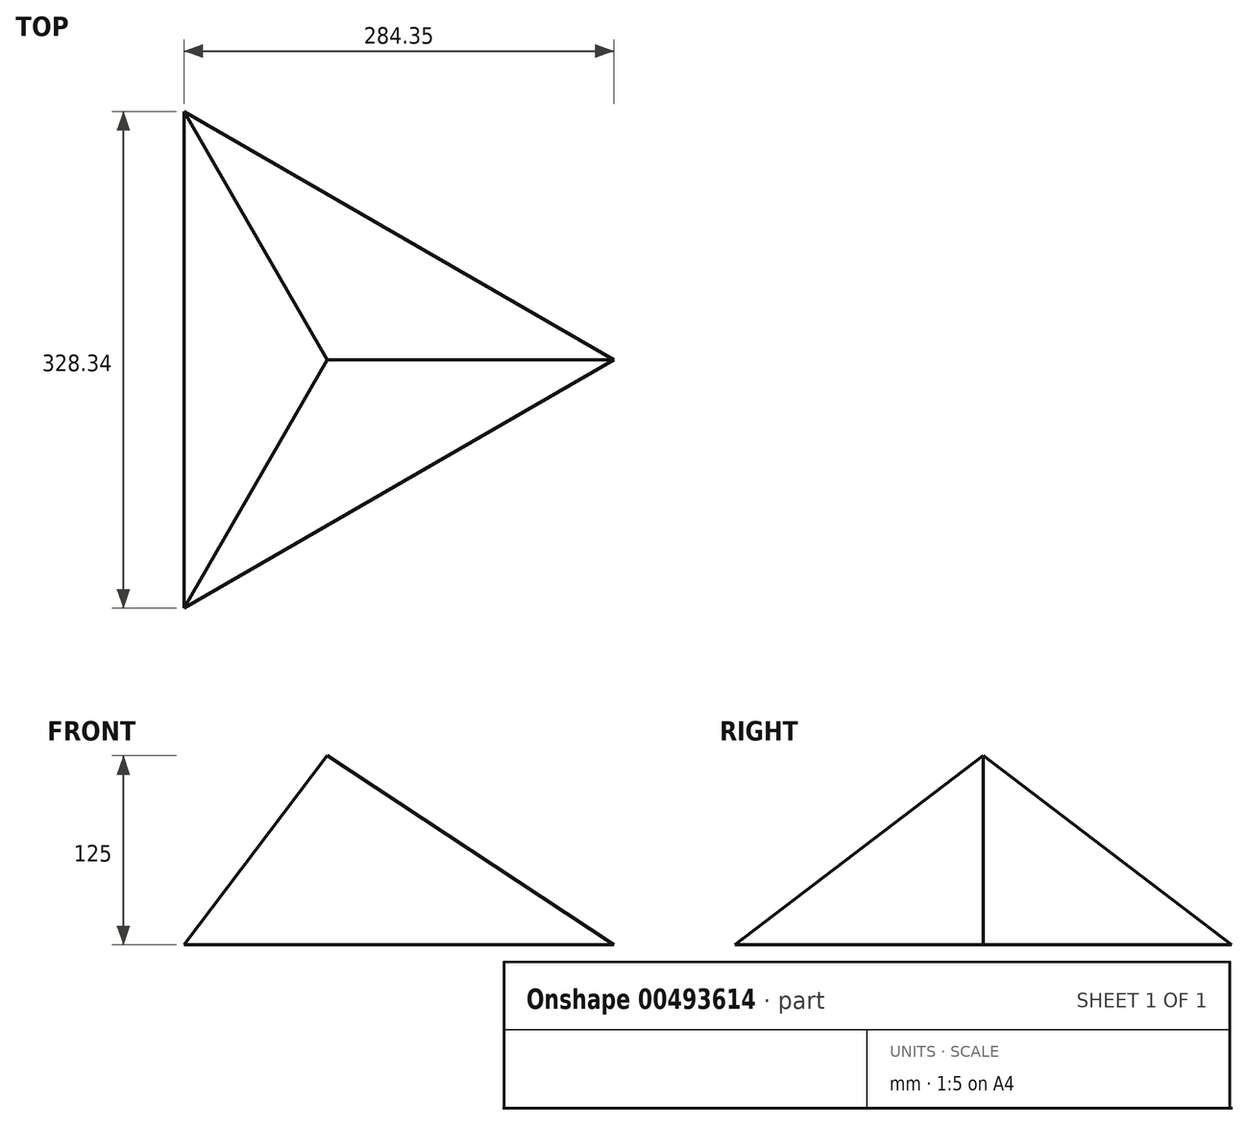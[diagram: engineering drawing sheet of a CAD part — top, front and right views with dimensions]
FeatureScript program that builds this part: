
annotation { "Feature Type Name" : "Feature", "Feature Type Description" : "" }
export const myFeature = defineFeature(function(context is Context, id is Id, definition is map)
    precondition{}
    {
        {
            var Q0;
            Q0=qCreatedBy(makeId("Top.planeOp"),FACE);
            var sketch = newSketch(context, id + "F0", { "sketchPlane" : qUnion([Q0])});
            skCircle(sketch, "E0.cCircle", {"center": v(0, 0) * mm, "radius": 189.57 * mm, "construction": true});
            skLineSegment(sketch, "E0.0", {"start": v(189.57, 0) * mm, "end": v(-94.78, -164.17) * mm});
            skLineSegment(sketch, "E0.1", {"start": v(-94.78, -164.17) * mm, "end": v(-94.78, 164.17) * mm});
            skLineSegment(sketch, "E0.2", {"start": v(-94.78, 164.17) * mm, "end": v(189.57, 0) * mm});
            skSolve(sketch);
        }
        {
            var Q0;
            Q0=qCreatedBy(makeId("Top.planeOp"),FACE);
            cPlane(context, id + "F1", {"entities" : qUnion([Q0]), "cplaneType" : CPlaneType.OFFSET, "offset" : 125 * mm, "width" : 150 * mm, "height" : 150 * mm});
        }
        {
            var Q0;
            Q0=qCreatedBy(id+"F1.planeOp",FACE);
            var sketch = newSketch(context, id + "F2", { "sketchPlane" : qUnion([Q0])});
            skPoint(sketch, "E1", {"position": v(0, 0) * mm});
            skSolve(sketch);
        }
        {
            var Q0;
            Q0=makeQuery(id+"F0.imprint","IMPRINT",FACE,{"disambiguationData":[TD([[makeQuery(id+"F0.imprint","IMPRINT",EDGE,{"derivedFrom":sQuery(id+"F0.wireOp",EDGE,"E0.0")}),-1.0]])]});
            var Q1;
            Q1=sQuery(id+"F2.wireOp",VERTEX,"E1");
            loft(context, id + "F3", {"sheetProfilesArray" : [{ "sheetProfileEntities" : qUnion([Q0]) }, { "sheetProfileEntities" : qUnion([Q1]) }]});
        }
    });
